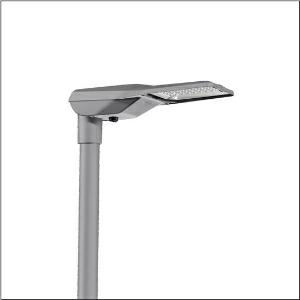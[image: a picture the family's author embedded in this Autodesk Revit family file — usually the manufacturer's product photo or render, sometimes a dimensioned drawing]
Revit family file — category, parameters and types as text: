
# Revit family: streetlight_sl_21_iq_mini___st1_0a_5xe2d31u08gb_76f1
name_source: partatom
category: Lighting Fixtures
units: mm (PartAtom-declared; Revit-internal decimal feet)

## family parameters
Cut with Voids When Loaded = No
Host = Face
Light Source = No
Part Type = Normal
Room Calculation Point = No
Round Connector Dimension = Use Diameter
Shared = No

## types (1)
- --- (1 x LED, 5990 lm, 39.8 W, 3000K)
    Apparent Load = 40 VA
    CIE Flux Codes = 37 72 97 100 100
    Color Rendering = 70
    Color Temperature = 3000K
    Default Elevation = 1800 mm
    Description = Streetlight SL 21 iQ mini, mast luminaire, primary light control with lens, of PMMA, primary optical cover: cover, of toughened safety glass, transparent, light distribution: ST1.0a, light emission: direct distribution, primary light characteristic: asymmetric, installation type: post-top, side-entry, LED, High Power LED, rated luminous flux: 5.990lm, luminous efficacy: 151lm/W, light colour: 730, colour temperature: 3000K, control: presetting dimming logarithmic, Street-Remote, Auto-Match, Temp-Guard, Lumen-Switch, Night-Set, Smart-Wire, Light-Fading, Desk-Remote (wireless, voltage-free reading and setting of iQ features in the workshop via application-optimized NFC function/RFID function), optimised constant luminous flux control (CLO 2.0), mains connection: 220..240V, AC, 50/60Hz, start of lifetime: 40W, end of service life: 41W, reduction: 18W, luminaire housing, of diecast aluminium, powder-coated, Siteco® metallic grey (DB 702S), corrosivity category C5 mid according to DIN EN ISO 12944, please order mast flange separately, inclination adjustable: 0°, 5°, 10°, 15°, sealing non-destructively replaceable, multi-level sealing system, length: 628mm, width: 235mm, height: 110mm, mast flange for spigot size: 42mm (side-entry): 5XC10008XM4, 60/48mm (side-entry/post-top): 5XC10108XM2, 76/60mm (side-entry/post-top): 5XC10108XM1, Smart Interface below, protection rating (complete): IP66, insulation class (complete): insulation class II (safety insulation), certification: CE, ENEC, ENEC+, VDE, impact resistance: IK09, permissible operating ambient temperature for outdoor applications: -40..+50°C, standard-compliant lighting for roads and squares, packaging unit: 1 piece

Light Distribution: ST1.0a
    Height = 110 mm
    Lamp = 1 x LED
    Lamp Light Flux = 5990 lm
    Lamp Power = 39.8 W
    Lamp count = 1
    Length = 625 mm
    Luminous efficacy = 151 lm/W
    Manufacturer = Siteco
    ModVariant = No
    Model = 5XE2D31U08GB
    Number of Poles = 1
    OnlyDefault = Yes
    Power Factor = 1
    Product Name = Streetlight SL 21 iQ mini | ST1.0a
    Product group = mast luminaire | pylon top
    ProductGroupID = 6100
    Protection Class = Protection class II
    Protection Degree = IP 66
    RLX_Detail_Level = 1
    RLX_Emergency_Light_Flux = 0 lm
    RLX_Emergency_Type = 0
    RLX_Emergency_Type_DB = No
    RlxData = <blob elided: 92321 chars, md5=4d5b6e32>
    Socket = socket
    Standby Power = 0 W
    System Light Flux = 5990 lm
    System Power = 40 W
    Type Comments = factory setting: luminous flux: 100 % | dim-lin: 254 | 800 mA
    Type Image = l_1003516.jpg
    URL = http://relux.com
    VarID = @adj_045265
    Voltage = 0 V
    Weight = 0.00 kg
    Width = 234 mm

## geometry (parser evidence)
native form markers: Blend x4, Sweep x11
no freeform markers — native parametric forms only
